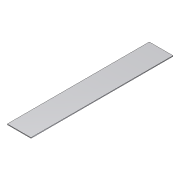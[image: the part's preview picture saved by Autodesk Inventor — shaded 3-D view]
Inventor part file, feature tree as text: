
AUTODESK INVENTOR PART (.ipt)
format: ipt  version: unknown  size: 159,744 bytes
history: native  units: in
note: dims shown in document units (in); Inventor stores cm internally (conversion verified against a paired STEP export)
features: extrude x1, sketch x1
ambient origin geometry x8: Origin, YZ Plane, XZ Plane, XY Plane, X Axis, Y Axis, Z Axis, Center Point
bodies: Solid1 (feature_tree)
feature tree (2):
  extrude  "Extrusion1"  Depth=8.0in
  sketch  "Sketch1"  dims[d0=0.25in d1=8.0in d2=48.0in d3=0.0in]
